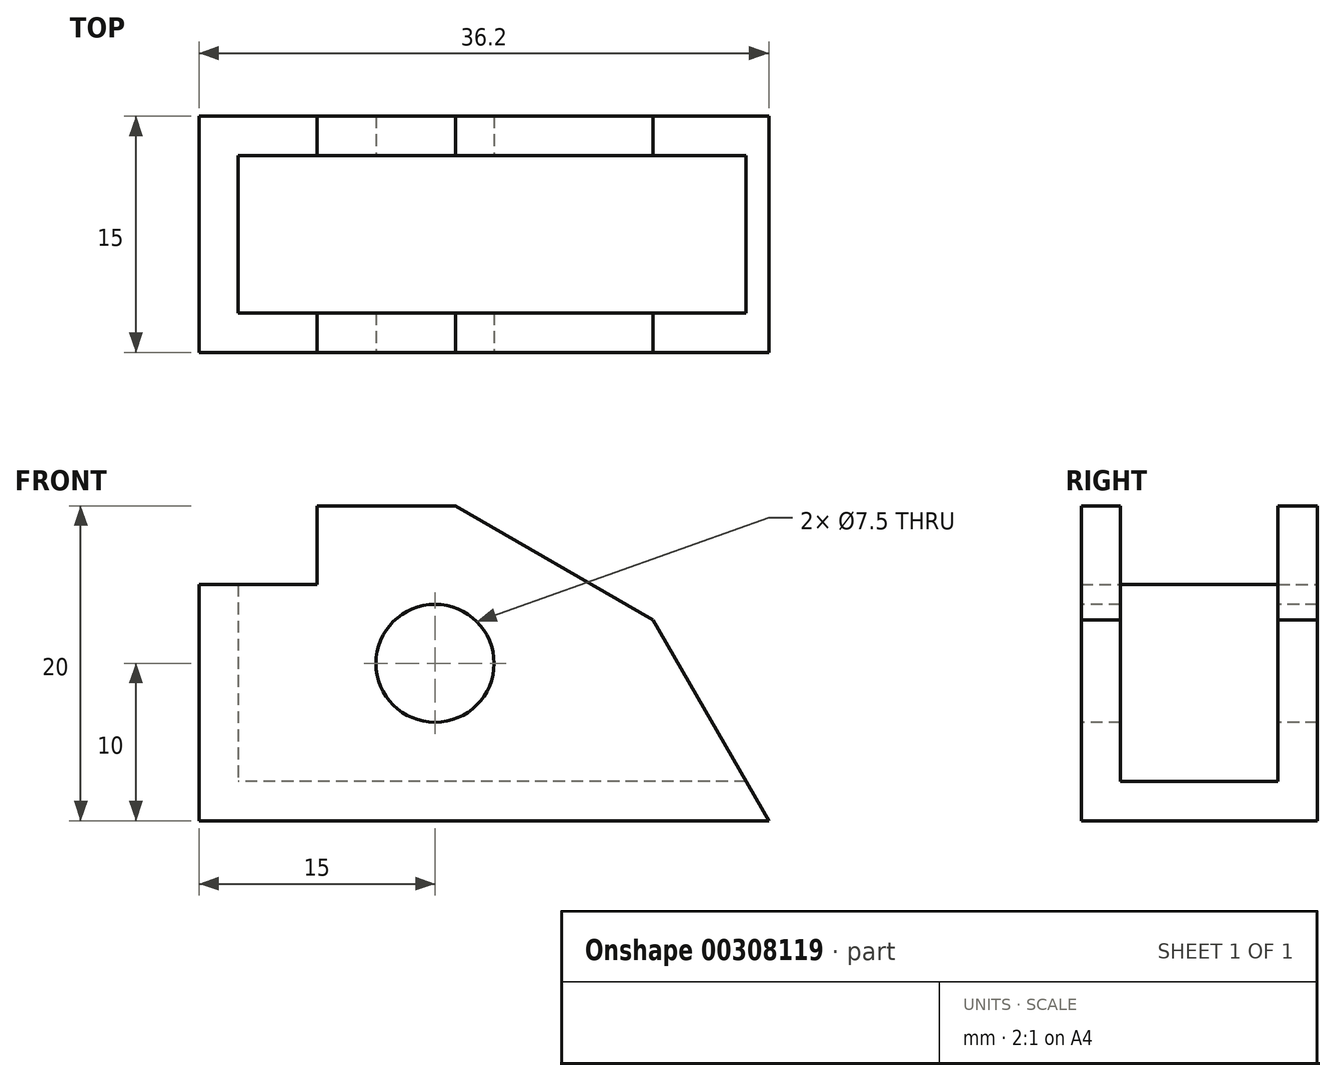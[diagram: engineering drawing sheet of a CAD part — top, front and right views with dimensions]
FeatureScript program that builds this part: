
annotation { "Feature Type Name" : "Feature", "Feature Type Description" : "" }
export const myFeature = defineFeature(function(context is Context, id is Id, definition is map)
    precondition{}
    {
        {
            var Q0;
            Q0=qCreatedBy(makeId("Front.planeOp"),FACE);
            var sketch = newSketch(context, id + "F0", { "sketchPlane" : qUnion([Q0])});
            skLineSegment(sketch, "E0", {"start": v(0, 0) * mm, "end": v(0, 15) * mm});
            skLineSegment(sketch, "E1", {"start": v(0, 15) * mm, "end": v(7.5, 15) * mm});
            skLineSegment(sketch, "E2", {"start": v(7.5, 15) * mm, "end": v(7.5, 20) * mm});
            skLineSegment(sketch, "E3", {"start": v(7.5, 20) * mm, "end": v(16.3, 20) * mm});
            skLineSegment(sketch, "E4", {"start": v(16.3, 20) * mm, "end": v(28.83, 12.77) * mm});
            skLineSegment(sketch, "E5", {"start": v(28.83, 12.77) * mm, "end": v(36.2, 0) * mm});
            skLineSegment(sketch, "E6", {"start": v(36.2, 0) * mm, "end": v(0, 0) * mm});
            skSolve(sketch);
        }
        {
            var Q0;
            Q0=makeQuery(id+"F0.imprint","IMPRINT",FACE,{"disambiguationData":[TD([[makeQuery(id+"F0.imprint","IMPRINT",EDGE,{"derivedFrom":sQuery(id+"F0.wireOp",EDGE,"E0")}),-1.0]])]});
            extrude(context, id + "F1", {"entities" : qUnion([Q0]), "depth" : 15 * mm});
        }
        {
            var Q0;
            Q0=qCreatedBy(makeId("Right.planeOp"),FACE);
            var sketch = newSketch(context, id + "F2", { "sketchPlane" : qUnion([Q0])});
            skLineSegment(sketch, "E7", {"start": v(-2.5, 2.5) * mm, "end": v(-2.5, 24.43) * mm});
            skLineSegment(sketch, "E8", {"start": v(-2.5, 24.43) * mm, "end": v(-12.5, 24.43) * mm});
            skLineSegment(sketch, "E9", {"start": v(-12.5, 24.43) * mm, "end": v(-12.5, 2.5) * mm});
            skLineSegment(sketch, "E10", {"start": v(-2.5, 2.5) * mm, "end": v(-12.5, 2.5) * mm});
            skPoint(sketch, "E11.orphan", {"position": v(-2.5, 0) * mm});
            skPoint(sketch, "E12.orphan", {"position": v(-12.5, 0) * mm});
            skSolve(sketch);
        }
        {
            var Q0;
            Q0=makeQuery(id+"F2.imprint","IMPRINT",FACE,{"disambiguationData":[TD([[makeQuery(id+"F2.imprint","IMPRINT",EDGE,{"derivedFrom":sQuery(id+"F2.wireOp",EDGE,"E7")}),1.0]])]});
            extrude(context, id + "F3", {"entities" : qUnion([Q0]), "operationType" : NewBodyOperationType.REMOVE, "depth" : 40 * mm});
        }
        {
            var Q0;
            Q0=makeQuery(id+"F3.boolean.opBoolean","COPY",FACE,{"derivedFrom":makeQuery(id+"F3.opExtrude","SWEPT_FACE",FACE,{"disambiguationData":[OSD([sQuery(id+"F2.wireOp",EDGE,"E10")])]})});
            var sketch = newSketch(context, id + "F4", { "sketchPlane" : qUnion([Q0])});
            skLineSegment(sketch, "E13", {"start": v(0, -12.5) * mm, "end": v(2.5, -12.5) * mm});
            skLineSegment(sketch, "E14", {"start": v(2.5, -12.5) * mm, "end": v(2.5, -2.5) * mm});
            skLineSegment(sketch, "E15", {"start": v(2.5, -2.5) * mm, "end": v(0, -2.5) * mm});
            skLineSegment(sketch, "E16", {"start": v(0, -2.5) * mm, "end": v(0, -12.5) * mm});
            skSolve(sketch);
        }
        {
            var Q0;
            Q0=makeQuery(id+"F4.imprint","IMPRINT",FACE,{"disambiguationData":[TD([[makeQuery(id+"F4.imprint","IMPRINT",EDGE,{"derivedFrom":sQuery(id+"F4.wireOp",EDGE,"E13")}),-1.0]])]});
            extrude(context, id + "F5", {"entities" : qUnion([Q0]), "operationType" : NewBodyOperationType.ADD, "depth" : 12.5 * mm});
        }
        {
            var Q0;
            Q0=makeQuery(id+"F1.opExtrude","CAP_FACE",FACE,{"disambiguationData":[OSD([sQuery(id+"F0.wireOp",EDGE,"E0"),sQuery(id+"F0.wireOp",EDGE,"E1"),sQuery(id+"F0.wireOp",EDGE,"E2"),sQuery(id+"F0.wireOp",EDGE,"E3"),sQuery(id+"F0.wireOp",EDGE,"E4"),sQuery(id+"F0.wireOp",EDGE,"E5"),sQuery(id+"F0.wireOp",EDGE,"E6")])],"isStart":false});
            var sketch = newSketch(context, id + "F6", { "sketchPlane" : qUnion([Q0])});
            skCircle(sketch, "E17", {"center": v(15, 10) * mm, "radius": 3.75 * mm});
            skSolve(sketch);
        }
        {
            var Q0;
            Q0=makeQuery(id+"F6.imprint","IMPRINT",FACE,{"disambiguationData":[TD([[makeQuery(id+"F6.imprint","IMPRINT",EDGE,{"derivedFrom":sQuery(id+"F6.wireOp",EDGE,"E17")}),1.0]])]});
            extrude(context, id + "F7", {"entities" : qUnion([Q0]), "operationType" : NewBodyOperationType.REMOVE, "oppositeDirection" : true, "depth" : 25 * mm});
        }
    });
